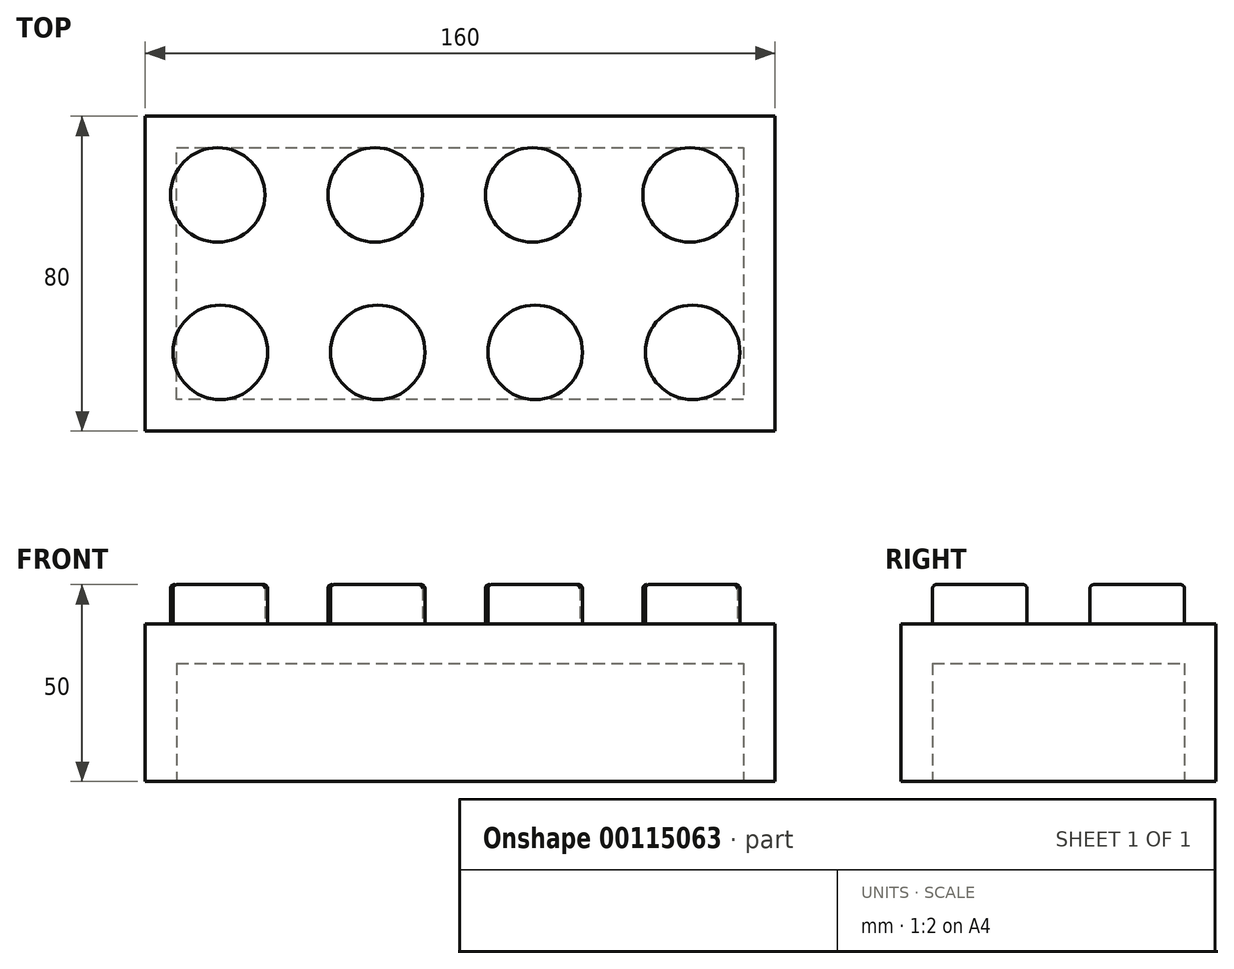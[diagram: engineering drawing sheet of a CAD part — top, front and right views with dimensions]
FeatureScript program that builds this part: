
annotation { "Feature Type Name" : "Feature", "Feature Type Description" : "" }
export const myFeature = defineFeature(function(context is Context, id is Id, definition is map)
    precondition{}
    {
        {
            var Q0;
            Q0=qCreatedBy(makeId("Top.planeOp"),FACE);
            var sketch = newSketch(context, id + "F0", { "sketchPlane" : qUnion([Q0])});
            skLineSegment(sketch, "E0.bottom", {"start": v(-113.85, 84.93) * mm, "end": v(46.15, 84.93) * mm});
            skLineSegment(sketch, "E0.top", {"start": v(-113.85, 4.93) * mm, "end": v(46.15, 4.93) * mm});
            skLineSegment(sketch, "E0.left", {"start": v(-113.85, 84.93) * mm, "end": v(-113.85, 4.93) * mm});
            skLineSegment(sketch, "E0.right", {"start": v(46.15, 84.93) * mm, "end": v(46.15, 4.93) * mm});
            skSolve(sketch);
        }
        {
            var Q0;
            Q0 = qSketchRegion(id + "F0", true);
            extrude(context, id + "F1", {"entities" : qUnion([Q0]), "depth" : 40 * mm});
        }
        {
            var Q0;
            Q0=makeQuery(id+"F1.opExtrude","CAP_FACE",FACE,{"disambiguationData":[OSD([sQuery(id+"F0.wireOp",EDGE,"E0.bottom"),sQuery(id+"F0.wireOp",EDGE,"E0.top"),sQuery(id+"F0.wireOp",EDGE,"E0.left"),sQuery(id+"F0.wireOp",EDGE,"E0.right")])],"isStart":true});
            var sketch = newSketch(context, id + "F2", { "sketchPlane" : qUnion([Q0])});
            skLineSegment(sketch, "E1.0", {"start": v(-105.85, -76.93) * mm, "end": v(38.15, -76.93) * mm});
            skLineSegment(sketch, "E1.1", {"start": v(-105.85, -12.93) * mm, "end": v(-105.85, -76.93) * mm});
            skLineSegment(sketch, "E1.2", {"start": v(38.15, -12.93) * mm, "end": v(-105.85, -12.93) * mm});
            skLineSegment(sketch, "E1.3", {"start": v(38.15, -76.93) * mm, "end": v(38.15, -12.93) * mm});
            skSolve(sketch);
        }
        {
            var Q0;
            Q0=makeQuery(id+"F2.imprint","IMPRINT",FACE,{"disambiguationData":[TD([[makeQuery(id+"F2.imprint","IMPRINT",EDGE,{"derivedFrom":sQuery(id+"F2.wireOp",EDGE,"E1.0")}),1.0]])]});
            extrude(context, id + "F3", {"entities" : qUnion([Q0]), "operationType" : NewBodyOperationType.REMOVE, "oppositeDirection" : true, "depth" : 30 * mm});
        }
        {
            var Q0;
            Q0=makeQuery(id+"F1.opExtrude","CAP_FACE",FACE,{"disambiguationData":[OSD([sQuery(id+"F0.wireOp",EDGE,"E0.bottom"),sQuery(id+"F0.wireOp",EDGE,"E0.top"),sQuery(id+"F0.wireOp",EDGE,"E0.left"),sQuery(id+"F0.wireOp",EDGE,"E0.right")])],"isStart":false});
            var sketch = newSketch(context, id + "F4", { "sketchPlane" : qUnion([Q0])});
            skCircle(sketch, "E2", {"center": v(-95.45, 64.93) * mm, "radius": 12 * mm});
            skCircle(sketch, "E3.0.1.0", {"center": v(-94.77, 24.94) * mm, "radius": 12 * mm});
            skCircle(sketch, "E3.1.0.0", {"center": v(-55.45, 64.93) * mm, "radius": 12 * mm});
            skCircle(sketch, "E3.1.1.0", {"center": v(-54.77, 24.94) * mm, "radius": 12 * mm});
            skCircle(sketch, "E3.2.0.0", {"center": v(-15.45, 64.93) * mm, "radius": 12 * mm});
            skCircle(sketch, "E3.2.1.0", {"center": v(-14.77, 24.94) * mm, "radius": 12 * mm});
            skCircle(sketch, "E3.3.0.0", {"center": v(24.55, 64.93) * mm, "radius": 12 * mm});
            skCircle(sketch, "E3.3.1.0", {"center": v(25.23, 24.94) * mm, "radius": 12 * mm});
            skLineSegment(sketch, "E3.direction1", {"start": v(-95.45, 64.93) * mm, "end": v(-55.45, 64.93) * mm, "construction": true});
            skLineSegment(sketch, "E3.direction2", {"start": v(-95.45, 64.93) * mm, "end": v(-94.77, 24.94) * mm, "construction": true});
            skSolve(sketch);
        }
        {
            var Q0;
            Q0 = qSketchRegion(id + "F4", true);
            extrude(context, id + "F5", {"entities" : qUnion([Q0]), "operationType" : NewBodyOperationType.ADD, "depth" : 10 * mm});
        }
        {
            var Q0;
            Q0=makeQuery(id+"F5.opExtrude","CAP_FACE",FACE,{"disambiguationData":[OSD([sQuery(id+"F4.wireOp",EDGE,"E2")])],"isStart":false});
            var Q1;
            Q1=makeQuery(id+"F5.opExtrude","CAP_FACE",FACE,{"disambiguationData":[OSD([sQuery(id+"F4.wireOp",EDGE,"E3.1.0.0")])],"isStart":false});
            var Q2;
            Q2=makeQuery(id+"F5.opExtrude","CAP_FACE",FACE,{"disambiguationData":[OSD([sQuery(id+"F4.wireOp",EDGE,"E3.2.0.0")])],"isStart":false});
            var Q3;
            Q3=makeQuery(id+"F5.opExtrude","CAP_FACE",FACE,{"disambiguationData":[OSD([sQuery(id+"F4.wireOp",EDGE,"E3.3.0.0")])],"isStart":false});
            var Q4;
            Q4=makeQuery(id+"F5.opExtrude","CAP_FACE",FACE,{"disambiguationData":[OSD([sQuery(id+"F4.wireOp",EDGE,"E3.0.1.0")])],"isStart":false});
            var Q5;
            Q5=makeQuery(id+"F5.opExtrude","CAP_FACE",FACE,{"disambiguationData":[OSD([sQuery(id+"F4.wireOp",EDGE,"E3.1.1.0")])],"isStart":false});
            var Q6;
            Q6=makeQuery(id+"F5.opExtrude","CAP_FACE",FACE,{"disambiguationData":[OSD([sQuery(id+"F4.wireOp",EDGE,"E3.2.1.0")])],"isStart":false});
            var Q7;
            Q7=makeQuery(id+"F5.opExtrude","CAP_FACE",FACE,{"disambiguationData":[OSD([sQuery(id+"F4.wireOp",EDGE,"E3.3.1.0")])],"isStart":false});
            fillet(context, id + "F6", {"entities" : qUnion([Q0, Q1, Q2, Q3, Q4, Q5, Q6, Q7]), "radius" : 1 * mm, "tangentPropagation" : true, "allowEdgeOverflow" : false});
        }
    });
